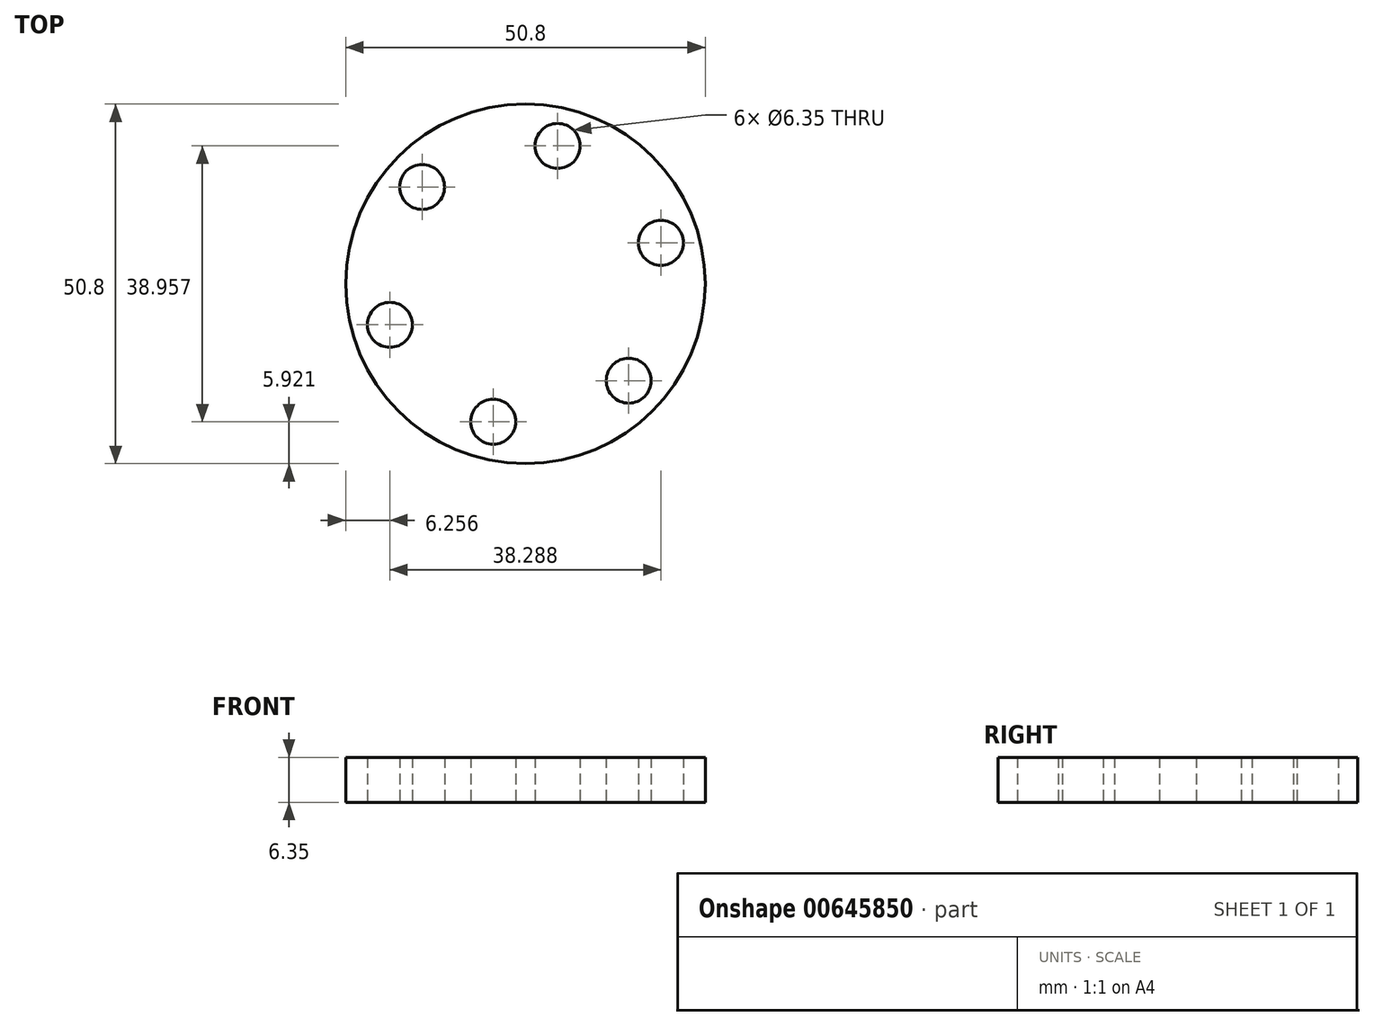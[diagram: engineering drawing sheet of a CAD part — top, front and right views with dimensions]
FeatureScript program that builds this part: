
annotation { "Feature Type Name" : "Feature", "Feature Type Description" : "" }
export const myFeature = defineFeature(function(context is Context, id is Id, definition is map)
    precondition{}
    {
        {
            var Q0;
            Q0=qCreatedBy(makeId("Top.planeOp"),FACE);
            var sketch = newSketch(context, id + "F0", { "sketchPlane" : qUnion([Q0])});
            skCircle(sketch, "E0", {"center": v(0, 0) * mm, "radius": 25.4 * mm});
            skCircle(sketch, "E1", {"center": v(4.55, 19.48) * mm, "radius": 3.18 * mm});
            skCircle(sketch, "E2.1.0", {"center": v(-14.6, 13.68) * mm, "radius": 3.18 * mm});
            skCircle(sketch, "E2.2.0", {"center": v(-19.14, -5.8) * mm, "radius": 3.18 * mm});
            skCircle(sketch, "E2.3.0", {"center": v(-4.55, -19.48) * mm, "radius": 3.18 * mm});
            skCircle(sketch, "E2.4.0", {"center": v(14.6, -13.68) * mm, "radius": 3.18 * mm});
            skCircle(sketch, "E2.5.0", {"center": v(19.14, 5.8) * mm, "radius": 3.18 * mm});
            skSolve(sketch);
        }
        {
            var Q0;
            Q0=makeQuery(id+"F0.imprint","IMPRINT",FACE,{"disambiguationData":[TD([[makeQuery(id+"F0.imprint","IMPRINT",EDGE,{"derivedFrom":sQuery(id+"F0.wireOp",EDGE,"E0")}),1.0]])]});
            extrude(context, id + "F1", {"entities" : qUnion([Q0]), "depth" : 6.35 * mm, "offsetDistance" : 25.4 * mm});
        }
    });
